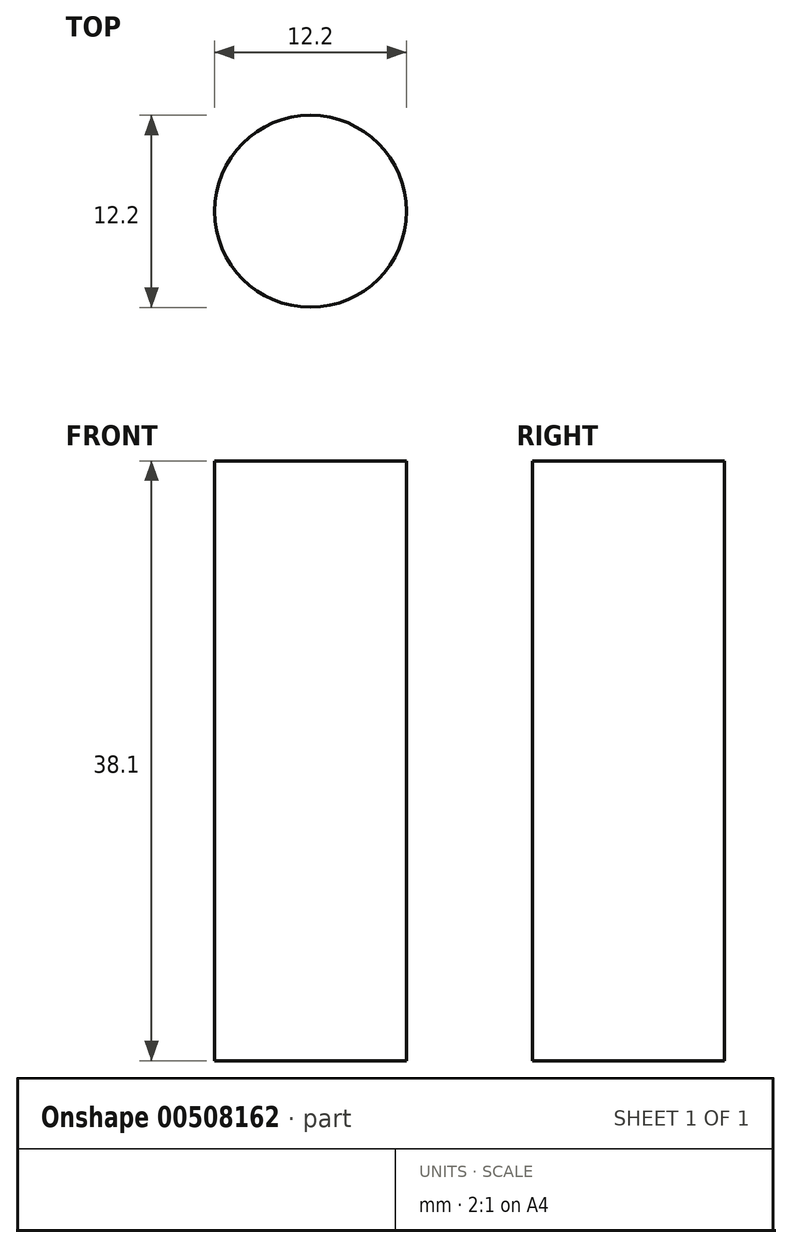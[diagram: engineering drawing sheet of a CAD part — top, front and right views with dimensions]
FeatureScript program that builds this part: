
annotation { "Feature Type Name" : "Feature", "Feature Type Description" : "" }
export const myFeature = defineFeature(function(context is Context, id is Id, definition is map)
    precondition{}
    {
        {
            var Q0;
            Q0=qCreatedBy(makeId("Top.planeOp"),FACE);
            var sketch = newSketch(context, id + "F0", { "sketchPlane" : qUnion([Q0])});
            skCircle(sketch, "E0", {"center": v(0, 0) * mm, "radius": 6.1 * mm});
            skSolve(sketch);
        }
        {
            var Q0;
            Q0=qSketchRegion(id+"F0",true);
            extrude(context, id + "F1", {"entities" : qUnion([Q0]), "depth" : 38.1 * mm});
        }
    });
